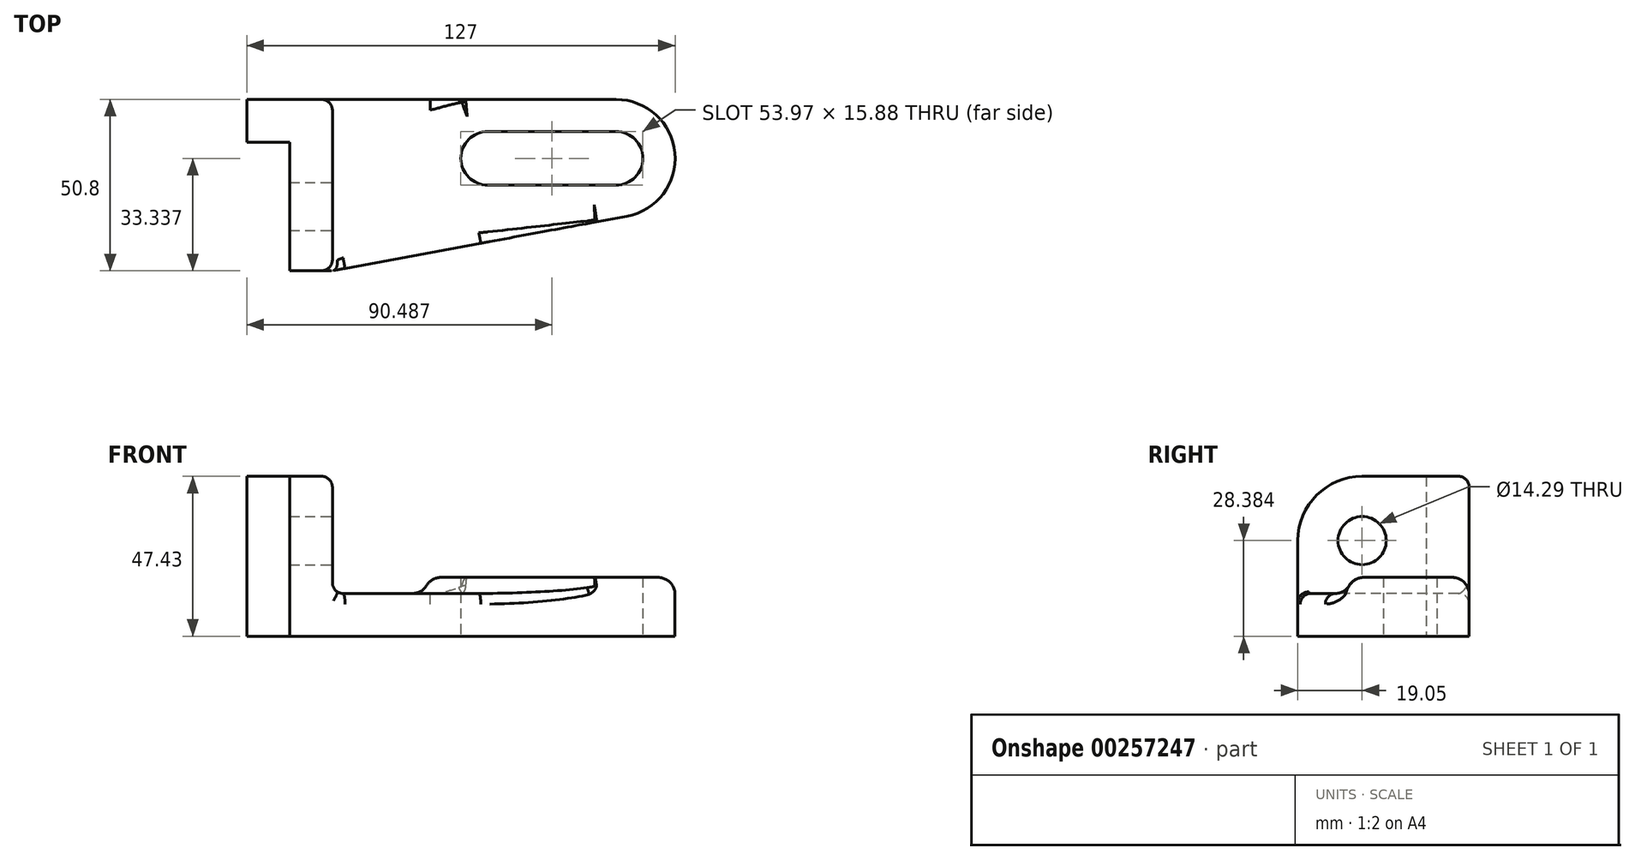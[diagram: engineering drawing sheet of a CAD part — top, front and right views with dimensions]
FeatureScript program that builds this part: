
annotation { "Feature Type Name" : "Feature", "Feature Type Description" : "" }
export const myFeature = defineFeature(function(context is Context, id is Id, definition is map)
    precondition{}
    {
        {
            var Q0;
            Q0=qCreatedBy(makeId("Top.planeOp"),FACE);
            var sketch = newSketch(context, id + "F0", { "sketchPlane" : qUnion([Q0])});
            skLineSegment(sketch, "E0.bottom", {"start": v(-39.3, 12.7) * mm, "end": v(57.54, 12.7) * mm});
            skLineSegment(sketch, "E0.top", {"start": v(19.44, -22.22) * mm, "end": v(57.54, -22.22) * mm});
            skArc(sketch, "E1", {"start": v(57.54, -22.22) * mm, "mid": v(75, -4.76) * mm, "end": v(57.54, 12.7) * mm});
            skLineSegment(sketch, "E2", {"start": v(60.72, -21.93) * mm, "end": v(-26.6, -38.1) * mm});
            skArc(sketch, "E3", {"start": v(19.44, 12.7) * mm, "mid": v(1.97, -4.76) * mm, "end": v(19.44, -22.22) * mm});
            skArc(sketch, "E4", {"start": v(57.54, -12.7) * mm, "mid": v(65.47, -4.76) * mm, "end": v(57.54, 3.18) * mm});
            skArc(sketch, "E5", {"start": v(19.44, 3.18) * mm, "mid": v(11.5, -4.76) * mm, "end": v(19.44, -12.7) * mm});
            skLineSegment(sketch, "E6", {"start": v(-26.6, -38.1) * mm, "end": v(-39.3, -38.1) * mm});
            skLineSegment(sketch, "E7", {"start": v(-39.3, 0) * mm, "end": v(-39.3, -38.1) * mm});
            skLineSegment(sketch, "E8", {"start": v(19.44, 3.18) * mm, "end": v(57.54, 3.18) * mm});
            skLineSegment(sketch, "E9", {"start": v(57.54, -12.7) * mm, "end": v(19.44, -12.7) * mm});
            skLineSegment(sketch, "E10", {"start": v(-26.6, -38.1) * mm, "end": v(-26.6, 12.7) * mm});
            skLineSegment(sketch, "E11", {"start": v(-39.3, 12.7) * mm, "end": v(-52, 12.7) * mm});
            skLineSegment(sketch, "E12", {"start": v(-52, 12.7) * mm, "end": v(-52, 0) * mm});
            skLineSegment(sketch, "E13", {"start": v(-52, 0) * mm, "end": v(-39.3, 0) * mm});
            skSolve(sketch);
        }
        {
            var Q0;
            Q0 = qSketchRegion(id + "F0", true);
            extrude(context, id + "F1", {"entities" : qUnion([Q0]), "depth" : 12.7 * mm});
        }
        {
            var Q0;
            Q0=makeQuery(id+"F0.imprint","IMPRINT",FACE,{"disambiguationData":[TD([[makeQuery(id+"F0.imprint","IMPRINT",EDGE,{"derivedFrom":sQuery(id+"F0.wireOp",EDGE,"E0.top")}),1.0]])]});
            extrude(context, id + "F2", {"entities" : qUnion([Q0]), "operationType" : NewBodyOperationType.ADD, "depth" : 17.46 * mm});
        }
        {
            var Q0;
            Q0=makeQuery(id+"F2.boolean.opBoolean","INTERSECT",EDGE,{"derivedFrom":[makeQuery(id+"F1.opExtrude","CAP_FACE",FACE,{"disambiguationData":[OSD([sQuery(id+"F0.wireOp",EDGE,"E0.bottom"),sQuery(id+"F0.wireOp",EDGE,"E1"),sQuery(id+"F0.wireOp",EDGE,"E2"),sQuery(id+"F0.wireOp",EDGE,"E4"),sQuery(id+"F0.wireOp",EDGE,"E5"),sQuery(id+"F0.wireOp",EDGE,"E6"),sQuery(id+"F0.wireOp",EDGE,"E7"),sQuery(id+"F0.wireOp",EDGE,"E8"),sQuery(id+"F0.wireOp",EDGE,"E9")])],"isStart":false}),makeQuery(id+"F2.opExtrude","SWEPT_FACE",FACE,{"disambiguationData":[OSD([sQuery(id+"F0.wireOp",EDGE,"E0.top")])]})]});
            fillet(context, id + "F3", {"entities" : qUnion([Q0]), "radius" : 4.76 * mm, "tangentPropagation" : true, "allowEdgeOverflow" : false});
        }
        {
            var Q0;
            Q0=makeQuery(id+"F0.imprint","IMPRINT",FACE,{"disambiguationData":[TD([[makeQuery(id+"F0.imprint","IMPRINT",EDGE,{"derivedFrom":sQuery(id+"F0.wireOp",EDGE,"E6")}),-1.0]])]});
            extrude(context, id + "F4", {"entities" : qUnion([Q0]), "operationType" : NewBodyOperationType.ADD, "depth" : 47.43 * mm});
        }
        {
            var Q0;
            Q0=makeQuery(id+"F4.opExtrude","CAP_EDGE",EDGE,{"disambiguationData":[OSD([sQuery(id+"F0.wireOp",EDGE,"E6")])],"isStart":false});
            fillet(context, id + "F5", {"entities" : qUnion([Q0]), "radius" : 19.05 * mm, "tangentPropagation" : true, "allowEdgeOverflow" : false});
        }
        {
            var Q0;
            Q0=makeQuery(id+"F4.opExtrude","SWEPT_EDGE",EDGE,{"disambiguationData":[OSD([sQuery(id+"F0.wireOp",EDGE,"E2"),sQuery(id+"F0.wireOp",EDGE,"E6"),sQuery(id+"F0.wireOp",EDGE,"E10")])]});
            var Q1;
            Q1=makeQuery(id+"F1.opExtrude","CAP_EDGE",EDGE,{"disambiguationData":[OSD([sQuery(id+"F0.wireOp",EDGE,"E2")])],"isStart":false});
            var Q2;
            Q2=makeQuery(id+"F4.boolean.opBoolean","INTERSECT",EDGE,{"derivedFrom":[makeQuery(id+"F1.opExtrude","CAP_FACE",FACE,{"disambiguationData":[OSD([sQuery(id+"F0.wireOp",EDGE,"E0.bottom"),sQuery(id+"F0.wireOp",EDGE,"E1"),sQuery(id+"F0.wireOp",EDGE,"E2"),sQuery(id+"F0.wireOp",EDGE,"E4"),sQuery(id+"F0.wireOp",EDGE,"E5"),sQuery(id+"F0.wireOp",EDGE,"E6"),sQuery(id+"F0.wireOp",EDGE,"E7"),sQuery(id+"F0.wireOp",EDGE,"E8"),sQuery(id+"F0.wireOp",EDGE,"E9"),sQuery(id+"F0.wireOp",EDGE,"E11"),sQuery(id+"F0.wireOp",EDGE,"E12"),sQuery(id+"F0.wireOp",EDGE,"E13")])],"isStart":false}),makeQuery(id+"F4.opExtrude","SWEPT_FACE",FACE,{"disambiguationData":[OSD([sQuery(id+"F0.wireOp",EDGE,"E10")])]})]});
            var Q3;
            Q3=makeQuery(id+"F1.opExtrude","SWEPT_EDGE",EDGE,{"disambiguationData":[OSD([sQuery(id+"F0.wireOp",EDGE,"E2"),sQuery(id+"F0.wireOp",EDGE,"E6"),sQuery(id+"F0.wireOp",EDGE,"E10")])]});
            fillet(context, id + "F6", {"entities" : qUnion([Q0, Q1, Q2, Q3]), "radius" : 3.17 * mm, "tangentPropagation" : true, "allowEdgeOverflow" : false});
        }
        {
            var Q0;
            Q0=makeQuery(id+"F4.opExtrude","CAP_EDGE",EDGE,{"disambiguationData":[OSD([sQuery(id+"F0.wireOp",EDGE,"E0.bottom"),sQuery(id+"F0.wireOp",EDGE,"E11")])],"isStart":false});
            var Q1;
            Q1=makeQuery(id+"F4.opExtrude","SWEPT_FACE",FACE,{"disambiguationData":[OSD([sQuery(id+"F0.wireOp",EDGE,"E10")])]});
            fillet(context, id + "F7", {"entities" : qUnion([Q0, Q1]), "radius" : 3.17 * mm, "tangentPropagation" : true, "allowEdgeOverflow" : false});
        }
        {
            var Q0;
            Q0=makeQuery(id+"F4.opExtrude","SWEPT_FACE",FACE,{"disambiguationData":[OSD([sQuery(id+"F0.wireOp",EDGE,"E10")])]});
            var sketch = newSketch(context, id + "F8", { "sketchPlane" : qUnion([Q0])});
            skCircle(sketch, "E14", {"center": v(-19.05, 28.38) * mm, "radius": 7.14 * mm});
            skSolve(sketch);
        }
        {
            var Q0;
            Q0=makeQuery(id+"F8.imprint","IMPRINT",FACE,{"disambiguationData":[TD([[makeQuery(id+"F8.imprint","IMPRINT",EDGE,{"derivedFrom":sQuery(id+"F8.wireOp",EDGE,"E14")}),1.0]])]});
            extrude(context, id + "F9", {"entities" : qUnion([Q0]), "operationType" : NewBodyOperationType.REMOVE, "endBound" : BoundingType.THROUGH_ALL, "oppositeDirection" : true, "depth" : 25.4 * mm});
        }
        {
            var Q0;
            {var subQ0=sQuery(id+"F0.wireOp",EDGE,"E2");var subQ1=makeQuery(id+"F1.opExtrude","SWEPT_FACE",FACE,{"disambiguationData":[OSD([subQ0])]});var subQ2=sQuery(id+"F0.wireOp",EDGE,"E1");Q0=makeQuery(id+"F6.opFillet","BLEND_EDGE",EDGE,{"blendedFrom":[makeQuery(id+"F3.opFillet","BLEND_EDGE",EDGE,{"blendedFrom":[makeQuery(id+"F2.boolean.opBoolean","INTERSECT",EDGE,{"derivedFrom":[makeQuery(id+"F1.opExtrude","CAP_FACE",FACE,{"disambiguationData":[OSD([sQuery(id+"F0.wireOp",EDGE,"E0.bottom"),subQ2,subQ0,sQuery(id+"F0.wireOp",EDGE,"E4"),sQuery(id+"F0.wireOp",EDGE,"E5"),sQuery(id+"F0.wireOp",EDGE,"E6"),sQuery(id+"F0.wireOp",EDGE,"E7"),sQuery(id+"F0.wireOp",EDGE,"E8"),sQuery(id+"F0.wireOp",EDGE,"E9"),sQuery(id+"F0.wireOp",EDGE,"E11"),sQuery(id+"F0.wireOp",EDGE,"E12"),sQuery(id+"F0.wireOp",EDGE,"E13")])],"isStart":false}),makeQuery(id+"F2.opExtrude","SWEPT_FACE",FACE,{"disambiguationData":[OSD([subQ2])]})]}),subQ1],"blendedInto":[subQ1]}),subQ1],"blendedInto":[subQ1]});}
            var Q1;
            {var subQ0=sQuery(id+"F0.wireOp",EDGE,"E13");var subQ1=sQuery(id+"F0.wireOp",EDGE,"E12");var subQ2=sQuery(id+"F0.wireOp",EDGE,"E11");var subQ3=sQuery(id+"F0.wireOp",EDGE,"E9");var subQ4=sQuery(id+"F0.wireOp",EDGE,"E8");var subQ5=sQuery(id+"F0.wireOp",EDGE,"E7");var subQ6=sQuery(id+"F0.wireOp",EDGE,"E6");var subQ7=sQuery(id+"F0.wireOp",EDGE,"E5");var subQ8=sQuery(id+"F0.wireOp",EDGE,"E4");var subQ9=sQuery(id+"F0.wireOp",EDGE,"E2");var subQ10=sQuery(id+"F0.wireOp",EDGE,"E1");var subQ11=sQuery(id+"F0.wireOp",EDGE,"E0.bottom");Q1=makeQuery(id+"F6.opFillet","BLEND_EDGE",EDGE,{"blendedFrom":[makeQuery(id+"F3.opFillet","BLEND_EDGE",EDGE,{"blendedFrom":[makeQuery(id+"F2.boolean.opBoolean","INTERSECT",EDGE,{"derivedFrom":[makeQuery(id+"F1.opExtrude","CAP_FACE",FACE,{"disambiguationData":[OSD([subQ11,subQ10,subQ9,subQ8,subQ7,subQ6,subQ5,subQ4,subQ3,subQ2,subQ1,subQ0])],"isStart":false}),makeQuery(id+"F2.opExtrude","SWEPT_FACE",FACE,{"disambiguationData":[OSD([subQ10])]})]}),makeQuery(id+"F1.opExtrude","SWEPT_FACE",FACE,{"disambiguationData":[OSD([subQ9])]})],"blendedInto":[makeQuery(id+"F1.opExtrude","SWEPT_FACE",FACE,{"disambiguationData":[OSD([subQ9])]})]}),makeQuery(id+"F3.opFillet","BLEND_FACE",FACE,{"disambiguationData":[OSD([subQ11,subQ10,subQ9,subQ8,subQ7,subQ6,subQ5,subQ4,subQ3,subQ2,subQ1,subQ0])]})],"blendedInto":[makeQuery(id+"F3.opFillet","BLEND_FACE",FACE,{"disambiguationData":[OSD([subQ11,subQ10,subQ9,subQ8,subQ7,subQ6,subQ5,subQ4,subQ3,subQ2,subQ1,subQ0])]})]});}
            var Q2;
            Q2=makeQuery(id+"F2.opExtrude","CAP_EDGE",EDGE,{"disambiguationData":[OSD([sQuery(id+"F0.wireOp",EDGE,"E1")])],"isStart":false});
            fillet(context, id + "F10", {"entities" : qUnion([Q0, Q1, Q2]), "radius" : 5.08 * mm, "tangentPropagation" : true, "allowEdgeOverflow" : false});
        }
    });
